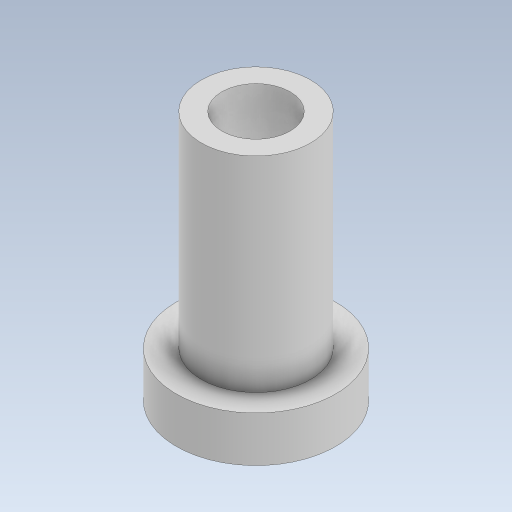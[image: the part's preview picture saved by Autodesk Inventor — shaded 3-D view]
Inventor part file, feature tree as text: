
AUTODESK INVENTOR PART (.ipt)
format: ipt  version: 2023.5 (Build 275446000, 446)  size: 273,408 bytes
history: native  units: mm
features: extrude x3, sketch x2
ambient origin geometry x8: Origin, YZ Plane, XZ Plane, XY Plane, X Axis, Y Axis, Z Axis, Center Point
bodies: Solid1 (feature_tree)
feature tree (5):
  sketch  "Sketch1"  dims[d0=4.8mm d1=7.0mm]
  extrude  "Extrusion1"  Depth=7.0mm
  extrude  "Extrusion2"  Depth=11.0mm TaperAngle=0.0deg
  extrude  "Extrusion3"  Depth=7.0mm
  sketch  "Sketch2"  dims[d2=2.0mm d3=0.0mm d4=11.0mm d5=0.0mm d6=3.0mm d7=7.0mm d8=0.0mm]
